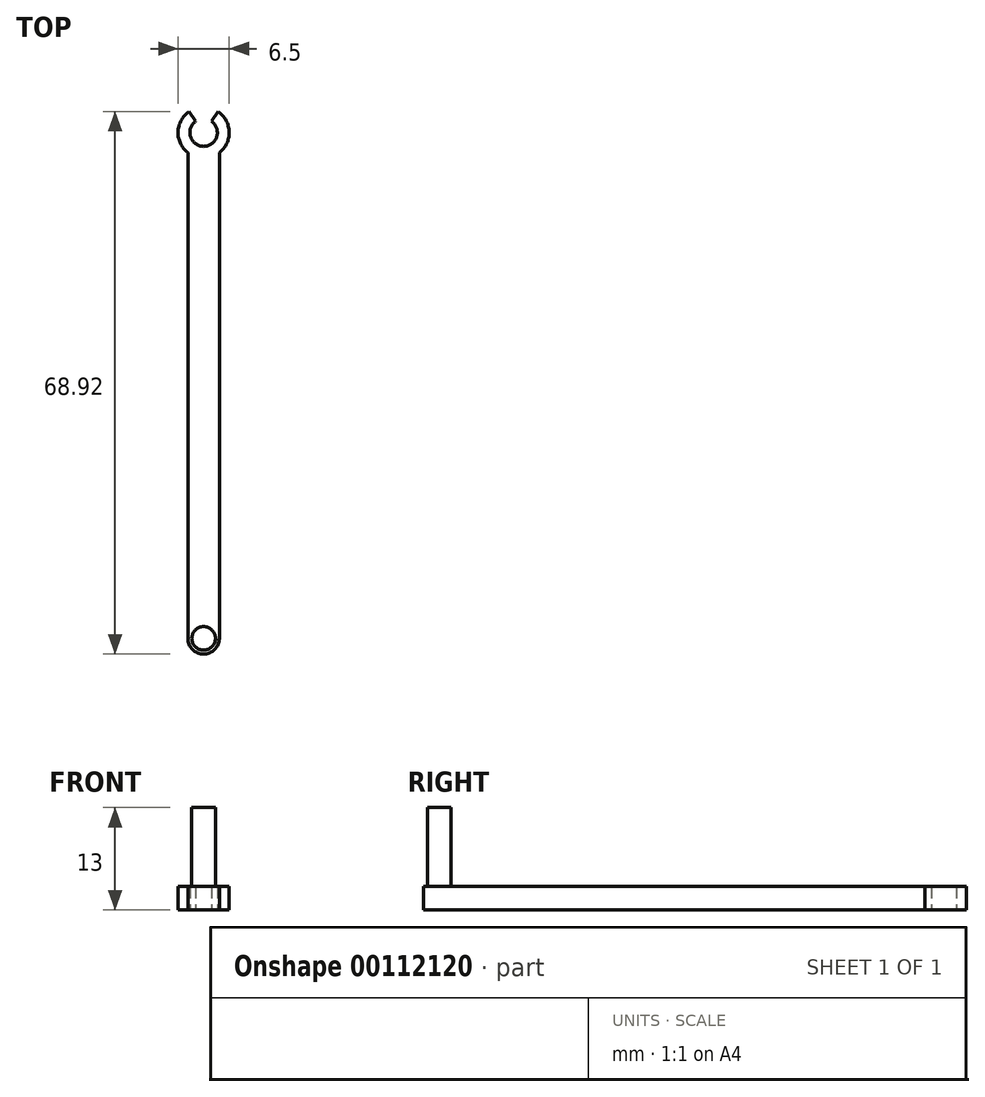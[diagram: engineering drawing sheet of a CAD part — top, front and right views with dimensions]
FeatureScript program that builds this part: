
annotation { "Feature Type Name" : "Feature", "Feature Type Description" : "" }
export const myFeature = defineFeature(function(context is Context, id is Id, definition is map)
    precondition{}
    {
        {
            var Q0;
            Q0=qCreatedBy(makeId("Top.planeOp"),FACE);
            var sketch = newSketch(context, id + "F0", { "sketchPlane" : qUnion([Q0])});
            skArc(sketch, "E0", {"start": v(1.4, 69.84) * mm, "mid": v(3.25, 63.92) * mm, "end": v(5.1, 69.84) * mm});
            skPoint(sketch, "E0.centerSnap0", {"position": v(3.25, 70.42) * mm});
            skArc(sketch, "E1", {"start": v(2.25, 68.61) * mm, "mid": v(3.25, 65.42) * mm, "end": v(4.25, 68.61) * mm});
            skLineSegment(sketch, "E2", {"start": v(3.25, 67.17) * mm, "end": v(5.1, 69.84) * mm});
            skLineSegment(sketch, "E3", {"start": v(3.25, 67.17) * mm, "end": v(1.4, 69.84) * mm});
            skLineSegment(sketch, "E4", {"start": v(2.25, 68.61) * mm, "end": v(4.25, 68.61) * mm});
            skLineSegment(sketch, "E5", {"start": v(3.25, 70.42) * mm, "end": v(3.25, 67.17) * mm});
            skLineSegment(sketch, "E6", {"start": v(3.25, 63.92) * mm, "end": v(3.25, 0.92) * mm});
            skLineSegment(sketch, "E7", {"start": v(1.25, 64.61) * mm, "end": v(1.25, 2.92) * mm});
            skLineSegment(sketch, "E8", {"start": v(5.25, 64.61) * mm, "end": v(5.25, 2.92) * mm});
            skPoint(sketch, "E9.orphan", {"position": v(0, 70.42) * mm});
            skPoint(sketch, "E10.trimOffspring.end.orphan", {"position": v(6.5, 70.42) * mm});
            skCircle(sketch, "E11", {"center": v(3.25, 2.92) * mm, "radius": 2 * mm});
            skSolve(sketch);
        }
        {
            var Q0;
            {var subQ1=sQuery(id+"F0.wireOp",EDGE,"7RT2il7h-merz-ThkM-nwO2-sf328oHhcdXs");var subQ7=makeQuery(id+"F0.imprint","INTERSECT",VERTEX,{"derivedFrom":[subQ1,sQuery(id+"F0.wireOp",EDGE,"E6")]});Q0=makeQuery(id+"F0.imprint","IMPRINT",FACE,{"disambiguationData":[TD([[makeQuery(id+"F0.imprint","IMPRINT",EDGE,{"disambiguationData":[TD([[subQ7,1.0]])],"derivedFrom":subQ1}),1.0]])]});}
            var Q1;
            {var subQ0=sQuery(id+"F0.wireOp",EDGE,"E6");Q1=makeQuery(id+"F0.imprint","IMPRINT",FACE,{"disambiguationData":[TD([[makeQuery(id+"F0.imprint","IMPRINT",EDGE,{"derivedFrom":subQ0}),-1.0]])]});}
            var Q2;
            {var subQ0=sQuery(id+"F0.wireOp",EDGE,"E6");Q2=makeQuery(id+"F0.imprint","IMPRINT",FACE,{"disambiguationData":[TD([[makeQuery(id+"F0.imprint","IMPRINT",EDGE,{"derivedFrom":subQ0}),1.0]])]});}
            var Q3;
            {var subQ8=sQuery(id+"F0.wireOp",EDGE,"E1");Q3=makeQuery(id+"F0.imprint","IMPRINT",FACE,{"disambiguationData":[TD([[makeQuery(id+"F0.imprint","IMPRINT",EDGE,{"derivedFrom":subQ8}),-1.0]])]});}
            var Q4;
            {var subQ3=sQuery(id+"F0.wireOp",EDGE,"E7");Q4=makeQuery(id+"F0.imprint","IMPRINT",FACE,{"disambiguationData":[TD([[makeQuery(id+"F0.imprint","IMPRINT",EDGE,{"derivedFrom":subQ3}),1.0]])]});}
            var Q5;
            {var subQ3=sQuery(id+"F0.wireOp",EDGE,"E8");Q5=makeQuery(id+"F0.imprint","IMPRINT",FACE,{"disambiguationData":[TD([[makeQuery(id+"F0.imprint","IMPRINT",EDGE,{"derivedFrom":subQ3}),-1.0]])]});}
            extrude(context, id + "F1", {"entities" : qUnion([Q0, Q1, Q2, Q3, Q4, Q5]), "depth" : 3 * mm});
        }
        {
            var Q0;
            Q0=makeQuery(id+"F1.opExtrude","CAP_FACE",FACE,{"disambiguationData":[OSD([sQuery(id+"F0.wireOp",EDGE,"E0"),sQuery(id+"F0.wireOp",EDGE,"E1"),sQuery(id+"F0.wireOp",EDGE,"E2"),sQuery(id+"F0.wireOp",EDGE,"E3"),sQuery(id+"F0.wireOp",EDGE,"E7"),sQuery(id+"F0.wireOp",EDGE,"E8"),sQuery(id+"F0.wireOp",EDGE,"E11")])],"isStart":false});
            var sketch = newSketch(context, id + "F2", { "sketchPlane" : qUnion([Q0])});
            skArc(sketch, "E12.0", {"start": v(1.25, 2.92) * mm, "mid": v(3.25, 0.92) * mm, "end": v(5.25, 2.92) * mm});
            skCircle(sketch, "E13", {"center": v(3.25, 2.92) * mm, "radius": 1.5 * mm});
            skSolve(sketch);
        }
        {
            var Q0;
            Q0=qSketchRegion(id+"F2",true);
            extrude(context, id + "F3", {"entities" : qUnion([Q0]), "operationType" : NewBodyOperationType.ADD, "depth" : 10 * mm});
        }
    });
